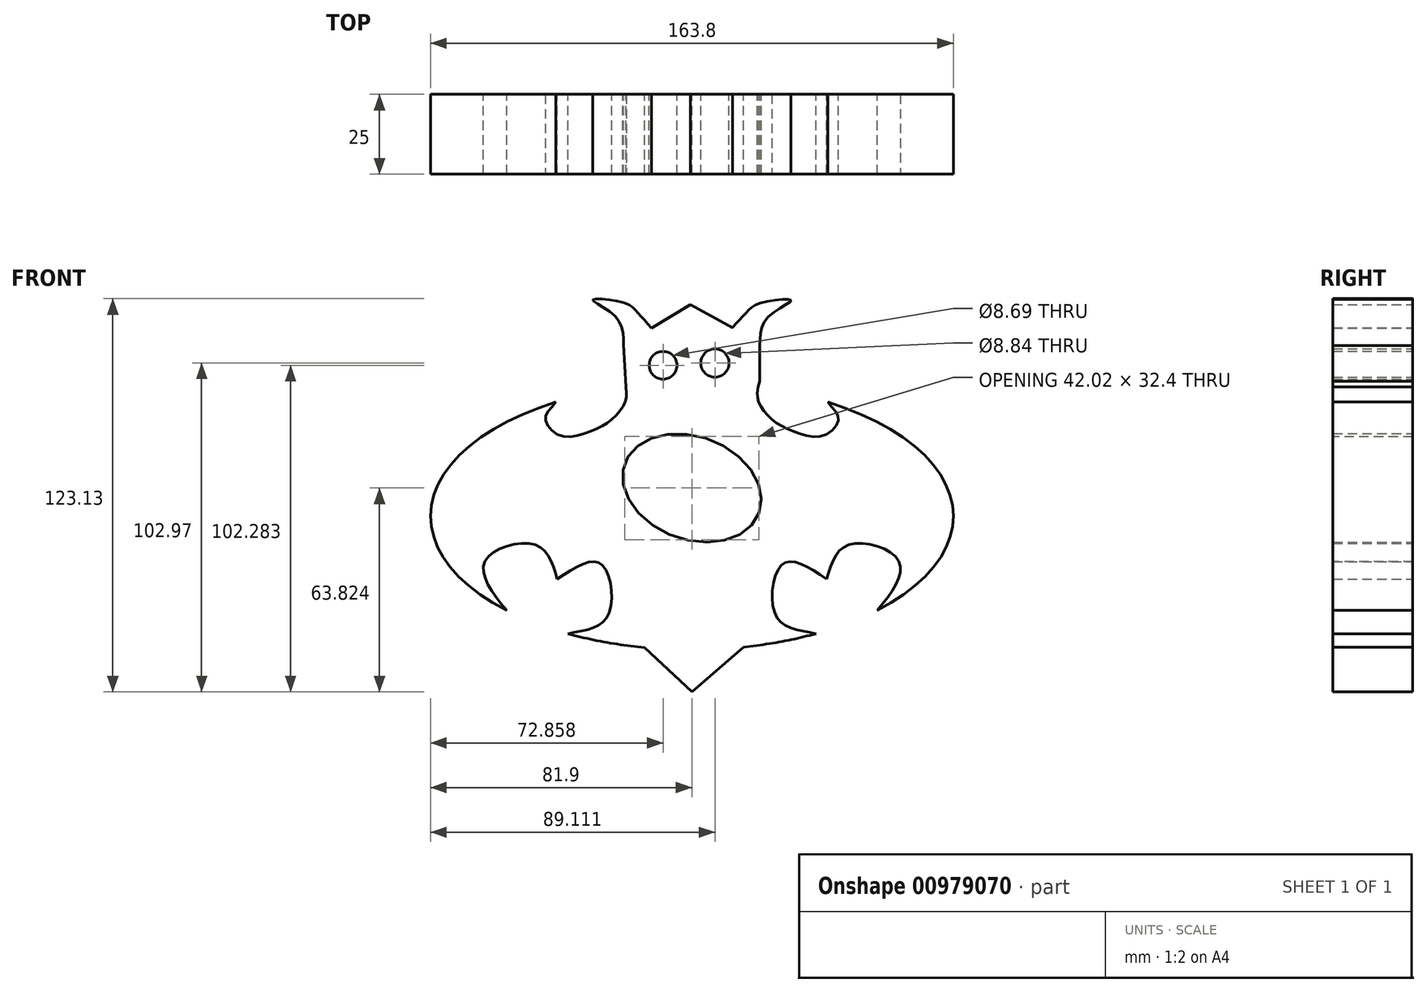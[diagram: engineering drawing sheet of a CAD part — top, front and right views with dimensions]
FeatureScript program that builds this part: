
annotation { "Feature Type Name" : "Feature", "Feature Type Description" : "" }
export const myFeature = defineFeature(function(context is Context, id is Id, definition is map)
    precondition{}
    {
        {
            var Q0;
            Q0=qCreatedBy(makeId("Front.planeOp"),FACE);
            var sketch = newSketch(context, id + "F0", { "sketchPlane" : qUnion([Q0])});
            skEllipticalArc(sketch, "E0", {});
            skFitSpline(sketch, "E1", {"points": [v(-58.05, -29.5) * mm, v(-64.78, -14.07) * mm, v(-49.2, -8.95) * mm, v(-42.21, -19.65) * mm], "startDerivative": vector(-39.09, 47.14) * mm, "endDerivative": vector(13.19, -45.71) * mm});
            skFitSpline(sketch, "E2", {"points": [v(-42.21, -19.65) * mm, v(-28.5, -15) * mm, v(-26.4, -31.28) * mm, v(-38.85, -36.82) * mm], "startDerivative": vector(48.46, 31.9) * mm, "endDerivative": vector(-48.67, -10.56) * mm});
            skPoint(sketch, "E3.endSnap0", {"position": v(0, -41.82) * mm});
            skFitSpline(sketch, "E4.MirrorCS", {"points": [v(58.05, -29.5) * mm, v(64.78, -14.07) * mm, v(49.2, -8.95) * mm, v(42.21, -19.65) * mm], "startDerivative": vector(39.09, 47.14) * mm, "endDerivative": vector(-13.19, -45.71) * mm});
            skFitSpline(sketch, "E5.MirrorCS", {"points": [v(42.21, -19.65) * mm, v(28.5, -15) * mm, v(26.4, -31.28) * mm, v(38.85, -36.82) * mm], "startDerivative": vector(-48.46, 31.9) * mm, "endDerivative": vector(48.67, -10.56) * mm});
            skFitSpline(sketch, "E6", {"points": [v(-42.58, 35.72) * mm, v(-45.94, 30.59) * mm, v(-41.28, 25.24) * mm, v(-31.52, 26.63) * mm, v(-25, 30.35) * mm, v(-21.05, 35.47) * mm, v(-20.67, 40.47) * mm], "startDerivative": vector(-29.66, -38.2) * mm, "endDerivative": vector(-6.17, 47.55) * mm});
            skFitSpline(sketch, "E7.MirrorCS", {"points": [v(42.58, 35.72) * mm, v(45.94, 30.59) * mm, v(41.28, 25.24) * mm, v(31.52, 26.63) * mm, v(25, 30.35) * mm, v(21.05, 35.47) * mm, v(20.67, 40.47) * mm], "startDerivative": vector(29.66, -38.2) * mm, "endDerivative": vector(6.17, 47.55) * mm});
            skLineSegment(sketch, "E8.3", {"start": v(-21.41, 53.64) * mm, "end": v(-21.13, 53.81) * mm});
            skLineSegment(sketch, "E8.4", {"start": v(-0.47, 66.27) * mm, "end": v(12.67, 59.02) * mm});
            skEllipticalArc(sketch, "E9.trimOffspring", {});
            skEllipticalArc(sketch, "E10.trimOffspring", {});
            skFitSpline(sketch, "E11", {"points": [v(-21.41, 53.64) * mm, v(-24.07, 62.68) * mm, v(-31.05, 67.8) * mm, v(-21.41, 66.87) * mm, v(-17.1, 63.85) * mm, v(-12.62, 58.95) * mm], "startDerivative": vector(-0.51, 44.03) * mm, "endDerivative": vector(26.3, -28.41) * mm});
            skFitSpline(sketch, "E12.MirrorCS", {"points": [v(21.27, 53.5) * mm, v(24, 62.52) * mm, v(31, 67.58) * mm, v(21.37, 66.72) * mm, v(17.03, 63.73) * mm, v(12.52, 58.86) * mm], "startDerivative": vector(0.82, 44.02) * mm, "endDerivative": vector(-26.49, -28.23) * mm});
            skLineSegment(sketch, "E13.trimOffspring", {"start": v(-12.62, 58.95) * mm, "end": v(-0.47, 66.27) * mm});
            skLineSegment(sketch, "E14", {"start": v(-14.78, -41.13) * mm, "end": v(0, -55) * mm});
            skLineSegment(sketch, "E15", {"start": v(0, -55) * mm, "end": v(16.13, -41) * mm});
            skEllipticalArc(sketch, "E16.trimOffspring", {});
            skLineSegment(sketch, "E17", {"start": v(-42.58, 35.72) * mm, "end": v(-44.13, 33.73) * mm});
            skLineSegment(sketch, "E18", {"start": v(-21.41, 53.64) * mm, "end": v(-20.67, 40.47) * mm});
            skPoint(sketch, "E19.orphan", {"position": v(20.95, 54.45) * mm});
            skPoint(sketch, "E8.cCircle.center.orphan", {"position": v(0, 41.82) * mm});
            skLineSegment(sketch, "E20", {"start": v(21.18, 42.22) * mm, "end": v(20.67, 40.47) * mm});
            skCircle(sketch, "E21", {"center": v(-9.04, 47.27) * mm, "radius": 4.34 * mm});
            skCircle(sketch, "E22", {"center": v(7.21, 47.96) * mm, "radius": 4.42 * mm});
            skLineSegment(sketch, "E23", {"start": v(21.27, 53.5) * mm, "end": v(21.18, 42.22) * mm});
            const initialGuessF0  = {"E0": [0, 0, -1, 0, 0.08190091736961719, 0.04181948385441519, 5.259104404308733, 0.7830960705082346], "E9.trimOffspring": [0, 0, -1, 0, 0.08190091736961719, 0.04181948385441519, 1.0766348496461298, 1.3892979187372163], "E10.trimOffspring": [0, 0, -1, 0, 0.08190091736961719, 0.04181948385441519, 2.358496583081563, 4.165673556460713], "E16.trimOffspring": [0, 0, -1, 0, 0.08190091736961719, 0.04181948385441519, 1.7690244559281902, 2.0649578039435945]};
            skSetInitialGuess(sketch, initialGuessF0);
            skSolve(sketch);
        }
        {
            var Q0;
            Q0 = qSketchRegion(id + "F0", true);
            extrude(context, id + "F1", {"entities" : qUnion([Q0]), "depth" : 25 * mm, "offsetDistance" : 25 * mm});
        }
        {
            var Q0;
            Q0=qCreatedBy(makeId("Front.planeOp"),FACE);
            var sketch = newSketch(context, id + "F2", { "sketchPlane" : qUnion([Q0])});
            skEllipse(sketch, "E24", {"center": v(0, 8.81) * mm, "majorRadius": 16.12 * mm, "minorRadius": 22.4 * mm, "majorAxis": v(-0.35, -0.94)});
            skSolve(sketch);
        }
        {
            var Q0;
            Q0 = qSketchRegion(id + "F2", true);
            extrude(context, id + "F3", {"entities" : qUnion([Q0]), "operationType" : NewBodyOperationType.REMOVE, "depth" : 89.1 * mm, "offsetDistance" : 25 * mm});
        }
    });
